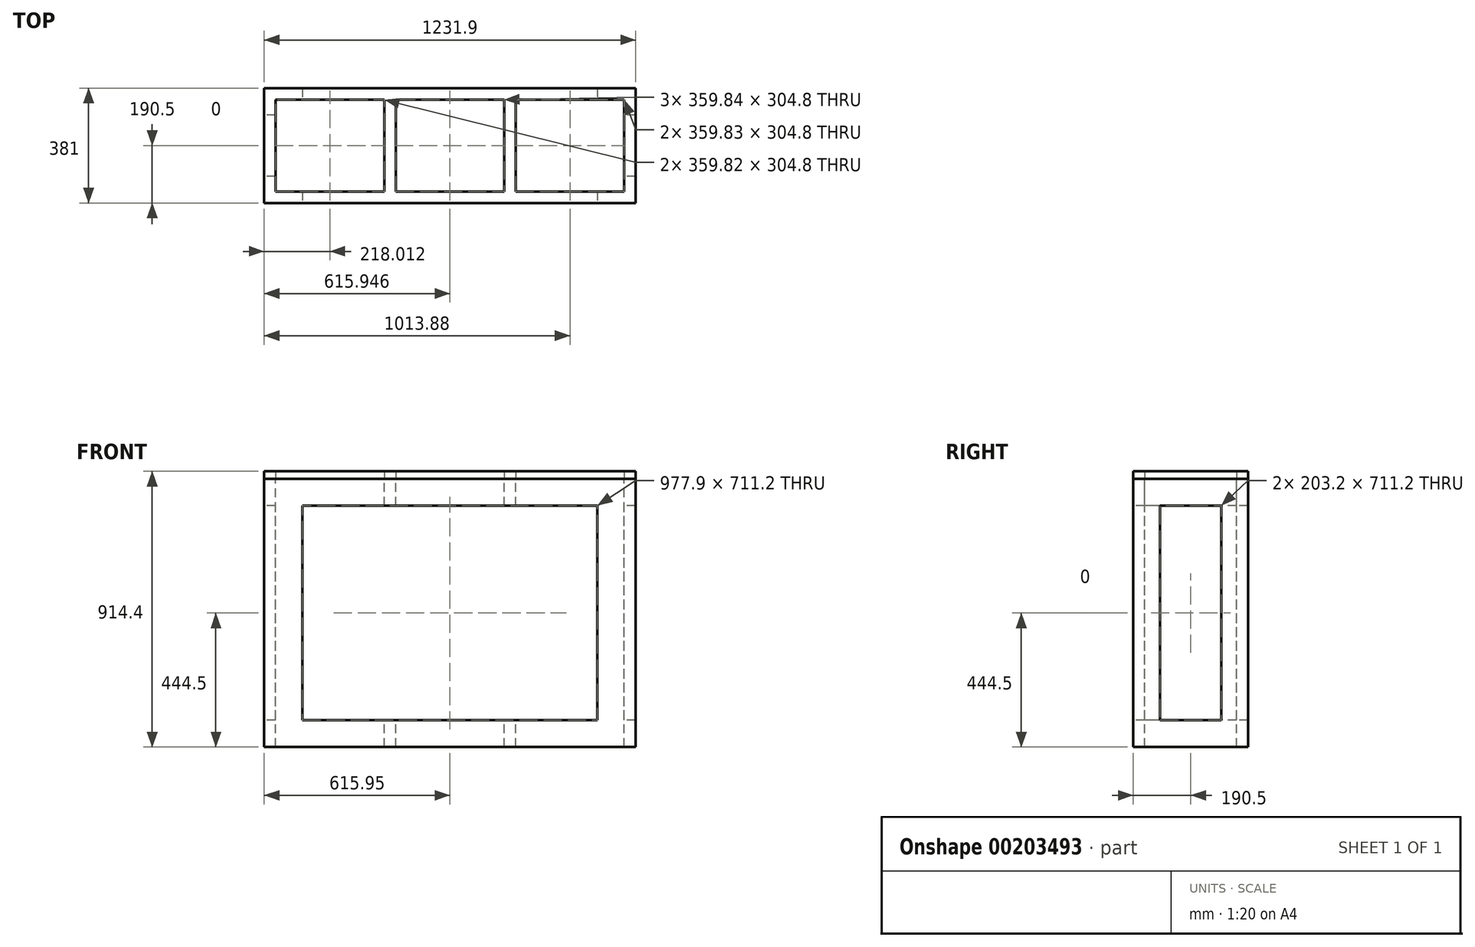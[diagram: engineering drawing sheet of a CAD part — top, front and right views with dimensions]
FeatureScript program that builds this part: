
annotation { "Feature Type Name" : "Feature", "Feature Type Description" : "" }
export const myFeature = defineFeature(function(context is Context, id is Id, definition is map)
    precondition{}
    {
        {
            var Q0;
            Q0=qCreatedBy(makeId("Top.planeOp"),FACE);
            var sketch = newSketch(context, id + "F0", { "sketchPlane" : qUnion([Q0])});
            skLineSegment(sketch, "E0.bottom", {"start": v(0, 0) * mm, "end": v(1231.9, 0) * mm});
            skLineSegment(sketch, "E0.top", {"start": v(0, 381) * mm, "end": v(1231.9, 381) * mm});
            skLineSegment(sketch, "E0.left", {"start": v(0, 0) * mm, "end": v(0, 381) * mm});
            skLineSegment(sketch, "E0.right", {"start": v(1231.9, 0) * mm, "end": v(1231.9, 381) * mm});
            skSolve(sketch);
        }
        {
            var Q0;
            Q0=makeQuery(id+"F0.imprint","IMPRINT",FACE,{"disambiguationData":[TD([[makeQuery(id+"F0.imprint","IMPRINT",EDGE,{"derivedFrom":sQuery(id+"F0.wireOp",EDGE,"E0.bottom")}),1.0]])]});
            extrude(context, id + "F6", {"entities" : qUnion([Q0]), "depth" : 889 * mm});
        }
        {
            var Q0;
            Q0=makeQuery(id+"F6.opExtrude","SWEPT_FACE",FACE,{"disambiguationData":[OSD([sQuery(id+"F0.wireOp",EDGE,"E0.left")])]});
            var sketch = newSketch(context, id + "F1", { "sketchPlane" : qUnion([Q0])});
            skLineSegment(sketch, "E1.bottom", {"start": v(-88.9, 800.1) * mm, "end": v(-292.1, 800.1) * mm});
            skLineSegment(sketch, "E1.top", {"start": v(-88.9, 88.9) * mm, "end": v(-292.1, 88.9) * mm});
            skLineSegment(sketch, "E1.left", {"start": v(-88.9, 800.1) * mm, "end": v(-88.9, 88.9) * mm});
            skLineSegment(sketch, "E1.right", {"start": v(-292.1, 800.1) * mm, "end": v(-292.1, 88.9) * mm});
            skSolve(sketch);
        }
        {
            var Q0;
            Q0=makeQuery(id+"F1.imprint","IMPRINT",FACE,{"disambiguationData":[TD([[makeQuery(id+"F1.imprint","IMPRINT",EDGE,{"derivedFrom":sQuery(id+"F1.wireOp",EDGE,"E1.bottom")}),1.0]])]});
            extrude(context, id + "F2", {"entities" : qUnion([Q0]), "operationType" : NewBodyOperationType.REMOVE, "endBound" : BoundingType.THROUGH_ALL, "oppositeDirection" : true, "depth" : 25.4 * mm});
        }
        {
            var Q0;
            Q0=makeQuery(id+"F6.opExtrude","SWEPT_FACE",FACE,{"disambiguationData":[OSD([sQuery(id+"F0.wireOp",EDGE,"E0.bottom")])]});
            var sketch = newSketch(context, id + "F3", { "sketchPlane" : qUnion([Q0])});
            skLineSegment(sketch, "E2.bottom", {"start": v(1104.9, 800.1) * mm, "end": v(127, 800.1) * mm});
            skLineSegment(sketch, "E2.top", {"start": v(1104.9, 88.9) * mm, "end": v(127, 88.9) * mm});
            skLineSegment(sketch, "E2.left", {"start": v(1104.9, 800.1) * mm, "end": v(1104.9, 88.9) * mm});
            skLineSegment(sketch, "E2.right", {"start": v(127, 800.1) * mm, "end": v(127, 88.9) * mm});
            skSolve(sketch);
        }
        {
            var Q0;
            Q0=makeQuery(id+"F3.imprint","IMPRINT",FACE,{"disambiguationData":[TD([[makeQuery(id+"F3.imprint","IMPRINT",EDGE,{"derivedFrom":sQuery(id+"F3.wireOp",EDGE,"E2.bottom")}),1.0]])]});
            extrude(context, id + "F7", {"entities" : qUnion([Q0]), "operationType" : NewBodyOperationType.REMOVE, "endBound" : BoundingType.THROUGH_ALL, "oppositeDirection" : true, "depth" : 25.4 * mm});
        }
        {
            var Q0;
            Q0=makeQuery(id+"F6.opExtrude","CAP_FACE",FACE,{"disambiguationData":[OSD([sQuery(id+"F0.wireOp",EDGE,"E0.bottom"),sQuery(id+"F0.wireOp",EDGE,"E0.top"),sQuery(id+"F0.wireOp",EDGE,"E0.left"),sQuery(id+"F0.wireOp",EDGE,"E0.right")])],"isStart":false});
            var sketch = newSketch(context, id + "F8", { "sketchPlane" : qUnion([Q0])});
            skLineSegment(sketch, "E3.bottom", {"start": v(38.1, 342.9) * mm, "end": v(397.92, 342.9) * mm});
            skLineSegment(sketch, "E3.top", {"start": v(38.1, 38.1) * mm, "end": v(397.92, 38.1) * mm});
            skLineSegment(sketch, "E3.left", {"start": v(38.1, 342.9) * mm, "end": v(38.1, 38.1) * mm});
            skLineSegment(sketch, "E3.right", {"start": v(397.92, 342.9) * mm, "end": v(397.92, 38.1) * mm});
            skLineSegment(sketch, "E4.bottom", {"start": v(833.97, 342.9) * mm, "end": v(1193.8, 342.9) * mm});
            skLineSegment(sketch, "E4.top", {"start": v(833.97, 38.1) * mm, "end": v(1193.8, 38.1) * mm});
            skLineSegment(sketch, "E4.left", {"start": v(833.97, 342.9) * mm, "end": v(833.97, 38.1) * mm});
            skLineSegment(sketch, "E4.right", {"start": v(1193.8, 342.9) * mm, "end": v(1193.8, 38.1) * mm});
            skLineSegment(sketch, "E5.bottom", {"start": v(436.02, 342.9) * mm, "end": v(795.87, 342.9) * mm});
            skLineSegment(sketch, "E5.top", {"start": v(436.02, 38.1) * mm, "end": v(795.87, 38.1) * mm});
            skLineSegment(sketch, "E5.left", {"start": v(436.02, 342.9) * mm, "end": v(436.02, 38.1) * mm});
            skLineSegment(sketch, "E5.right", {"start": v(795.87, 342.9) * mm, "end": v(795.87, 38.1) * mm});
            skSolve(sketch);
        }
        {
            var Q0;
            Q0=makeQuery(id+"F8.imprint","IMPRINT",FACE,{"disambiguationData":[TD([[makeQuery(id+"F8.imprint","IMPRINT",EDGE,{"derivedFrom":sQuery(id+"F8.wireOp",EDGE,"E3.bottom")}),-1.0]])]});
            var Q1;
            Q1=makeQuery(id+"F8.imprint","IMPRINT",FACE,{"disambiguationData":[TD([[makeQuery(id+"F8.imprint","IMPRINT",EDGE,{"derivedFrom":sQuery(id+"F8.wireOp",EDGE,"E5.bottom")}),-1.0]])]});
            var Q2;
            Q2=makeQuery(id+"F8.imprint","IMPRINT",FACE,{"disambiguationData":[TD([[makeQuery(id+"F8.imprint","IMPRINT",EDGE,{"derivedFrom":sQuery(id+"F8.wireOp",EDGE,"E4.bottom")}),-1.0]])]});
            extrude(context, id + "F9", {"entities" : qUnion([Q0, Q1, Q2]), "operationType" : NewBodyOperationType.REMOVE, "endBound" : BoundingType.THROUGH_ALL, "oppositeDirection" : true, "depth" : 25.4 * mm});
        }
        {
            var Q0;
            Q0=makeQuery(id+"F6.opExtrude","CAP_FACE",FACE,{"disambiguationData":[OSD([sQuery(id+"F0.wireOp",EDGE,"E0.bottom"),sQuery(id+"F0.wireOp",EDGE,"E0.top"),sQuery(id+"F0.wireOp",EDGE,"E0.left"),sQuery(id+"F0.wireOp",EDGE,"E0.right")])],"isStart":false});
            var sketch = newSketch(context, id + "F4", { "sketchPlane" : qUnion([Q0])});
            skLineSegment(sketch, "E6.bottom", {"start": v(0, 0) * mm, "end": v(1231.9, 0) * mm});
            skLineSegment(sketch, "E6.top", {"start": v(0, 381) * mm, "end": v(1231.9, 381) * mm});
            skLineSegment(sketch, "E6.left", {"start": v(0, 0) * mm, "end": v(0, 381) * mm});
            skLineSegment(sketch, "E6.right", {"start": v(1231.9, 0) * mm, "end": v(1231.9, 381) * mm});
            skSolve(sketch);
        }
        {
            var Q0;
            Q0=makeQuery(id+"F4.imprint","IMPRINT",FACE,{"disambiguationData":[TD([[makeQuery(id+"F4.imprint","IMPRINT",EDGE,{"derivedFrom":sQuery(id+"F4.wireOp",EDGE,"E6.bottom")}),1.0]])]});
            var Q1;
            Q1=makeQuery(id+"F4.imprint","IMPRINT",FACE,{"disambiguationData":[TD([[makeQuery(id+"F4.imprint","IMPRINT",EDGE,{"derivedFrom":makeQuery(id+"F9.boolean.opBoolean","COPY",EDGE,{"derivedFrom":makeQuery(id+"F9.opExtrude","CAP_EDGE",EDGE,{"disambiguationData":[OSD([sQuery(id+"F8.wireOp",EDGE,"E4.bottom")])],"isStart":true})})}),-1.0]])]});
            var Q2;
            Q2=makeQuery(id+"F4.imprint","IMPRINT",FACE,{"disambiguationData":[TD([[makeQuery(id+"F4.imprint","IMPRINT",EDGE,{"derivedFrom":makeQuery(id+"F9.boolean.opBoolean","COPY",EDGE,{"derivedFrom":makeQuery(id+"F9.opExtrude","CAP_EDGE",EDGE,{"disambiguationData":[OSD([sQuery(id+"F8.wireOp",EDGE,"E5.bottom")])],"isStart":true})})}),-1.0]])]});
            var Q3;
            Q3=makeQuery(id+"F4.imprint","IMPRINT",FACE,{"disambiguationData":[TD([[makeQuery(id+"F4.imprint","IMPRINT",EDGE,{"derivedFrom":makeQuery(id+"F9.boolean.opBoolean","COPY",EDGE,{"derivedFrom":makeQuery(id+"F9.opExtrude","CAP_EDGE",EDGE,{"disambiguationData":[OSD([sQuery(id+"F8.wireOp",EDGE,"E3.bottom")])],"isStart":true})})}),-1.0]])]});
            extrude(context, id + "F5", {"entities" : qUnion([Q0, Q1, Q2, Q3]), "depth" : 25.4 * mm});
        }
    });
